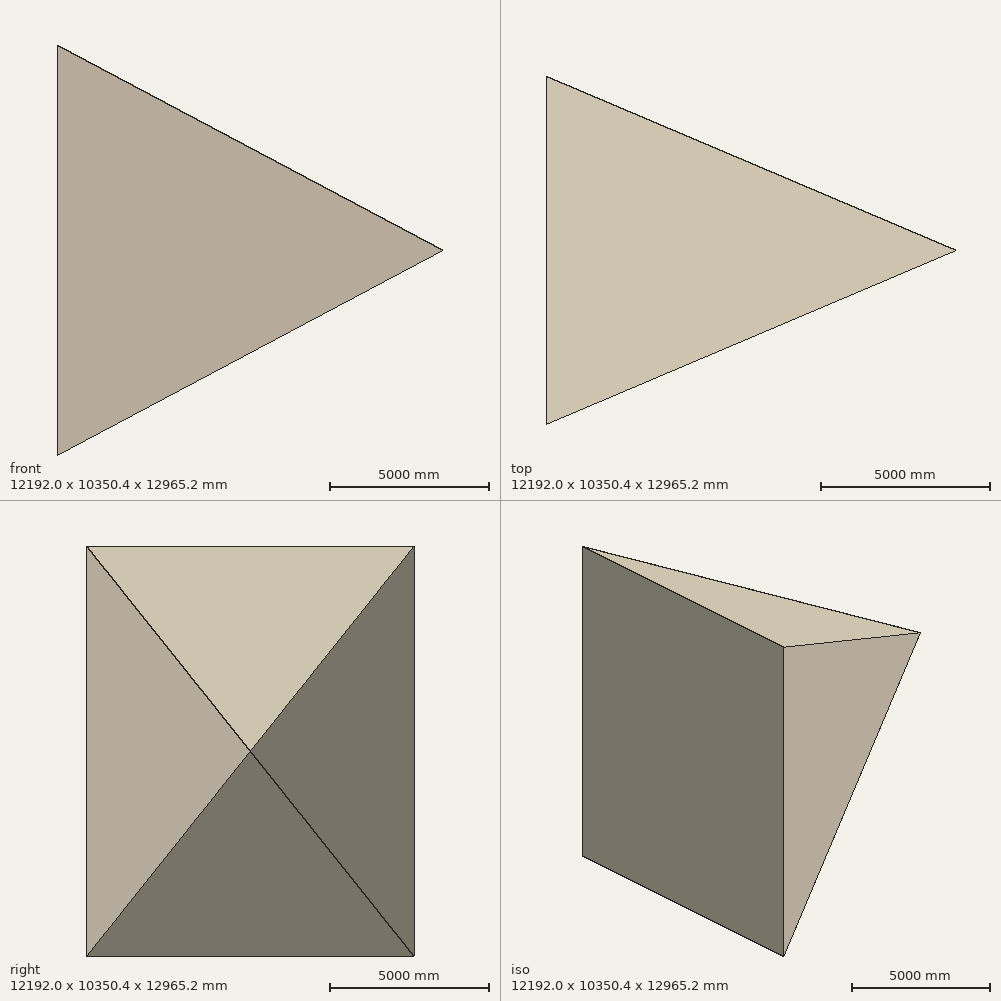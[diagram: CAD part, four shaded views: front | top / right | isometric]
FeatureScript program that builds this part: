
annotation { "Feature Type Name" : "Feature", "Feature Type Description" : "" }
export const myFeature = defineFeature(function(context is Context, id is Id, definition is map)
    precondition{}
    {
        {
            var Q0;
            Q0=qCreatedBy(makeId("Front.planeOp"),FACE);
            var sketch = newSketch(context, id + "F0", { "sketchPlane" : qUnion([Q0])});
            skLineSegment(sketch, "E0", {"start": v(0, 0) * mm, "end": v(-12192, 6482.6) * mm});
            skLineSegment(sketch, "E1", {"start": v(-12192, 6482.6) * mm, "end": v(-12192, -6482.6) * mm});
            skLineSegment(sketch, "E2", {"start": v(-12192, -6482.6) * mm, "end": v(0, 0) * mm});
            skSolve(sketch);
        }
        {
            var Q0;
            Q0=qCreatedBy(makeId("Top.planeOp"),FACE);
            var sketch = newSketch(context, id + "F1", { "sketchPlane" : qUnion([Q0])});
            skLineSegment(sketch, "E3", {"start": v(0, 0) * mm, "end": v(-12192, 5175.2) * mm});
            skLineSegment(sketch, "E4", {"start": v(-12192, 5175.2) * mm, "end": v(-12192, -5175.2) * mm});
            skLineSegment(sketch, "E5", {"start": v(-12192, -5175.2) * mm, "end": v(0, 0) * mm});
            skSolve(sketch);
        }
        {
            var Q0;
            Q0=makeQuery(id+"F0.imprint","IMPRINT",FACE,{"disambiguationData":[TD([[makeQuery(id+"F0.imprint","IMPRINT",EDGE,{"derivedFrom":sQuery(id+"F0.wireOp",EDGE,"E0")}),1.0]])]});
            var Q1;
            Q1=sQuery(id+"F1.wireOp",VERTEX,"E5.start");
            var Q2;
            Q2=sQuery(id+"F1.wireOp",VERTEX,"E4.start");
            extrude(context, id + "F2", {"entities" : qUnion([Q0]), "endBound" : BoundingType.UP_TO_VERTEX, "endBoundEntityVertex" : qUnion([Q1]), "depth" : 25.4 * mm, "hasSecondDirection" : true, "secondDirectionBound" : SecondDirectionBoundingType.UP_TO_VERTEX, "secondDirectionOppositeDirection" : true, "secondDirectionBoundEntityVertex" : qUnion([Q2]), "secondDirectionDepth" : 25.4 * mm});
        }
        {
            var Q0;
            Q0 = qSketchRegion(id + "F1", true);
            var Q1;
            Q1=sQuery(id+"F0.wireOp",VERTEX,"E1.start");
            var Q2;
            Q2=sQuery(id+"F0.wireOp",VERTEX,"E2.start");
            extrude(context, id + "F3", {"entities" : qUnion([Q0]), "operationType" : NewBodyOperationType.INTERSECT, "endBound" : BoundingType.UP_TO_VERTEX, "endBoundEntityVertex" : qUnion([Q1]), "depth" : 25.4 * mm, "hasSecondDirection" : true, "secondDirectionBound" : SecondDirectionBoundingType.UP_TO_VERTEX, "secondDirectionOppositeDirection" : true, "secondDirectionBoundEntityVertex" : qUnion([Q2]), "secondDirectionDepth" : 25.4 * mm});
        }
    });
